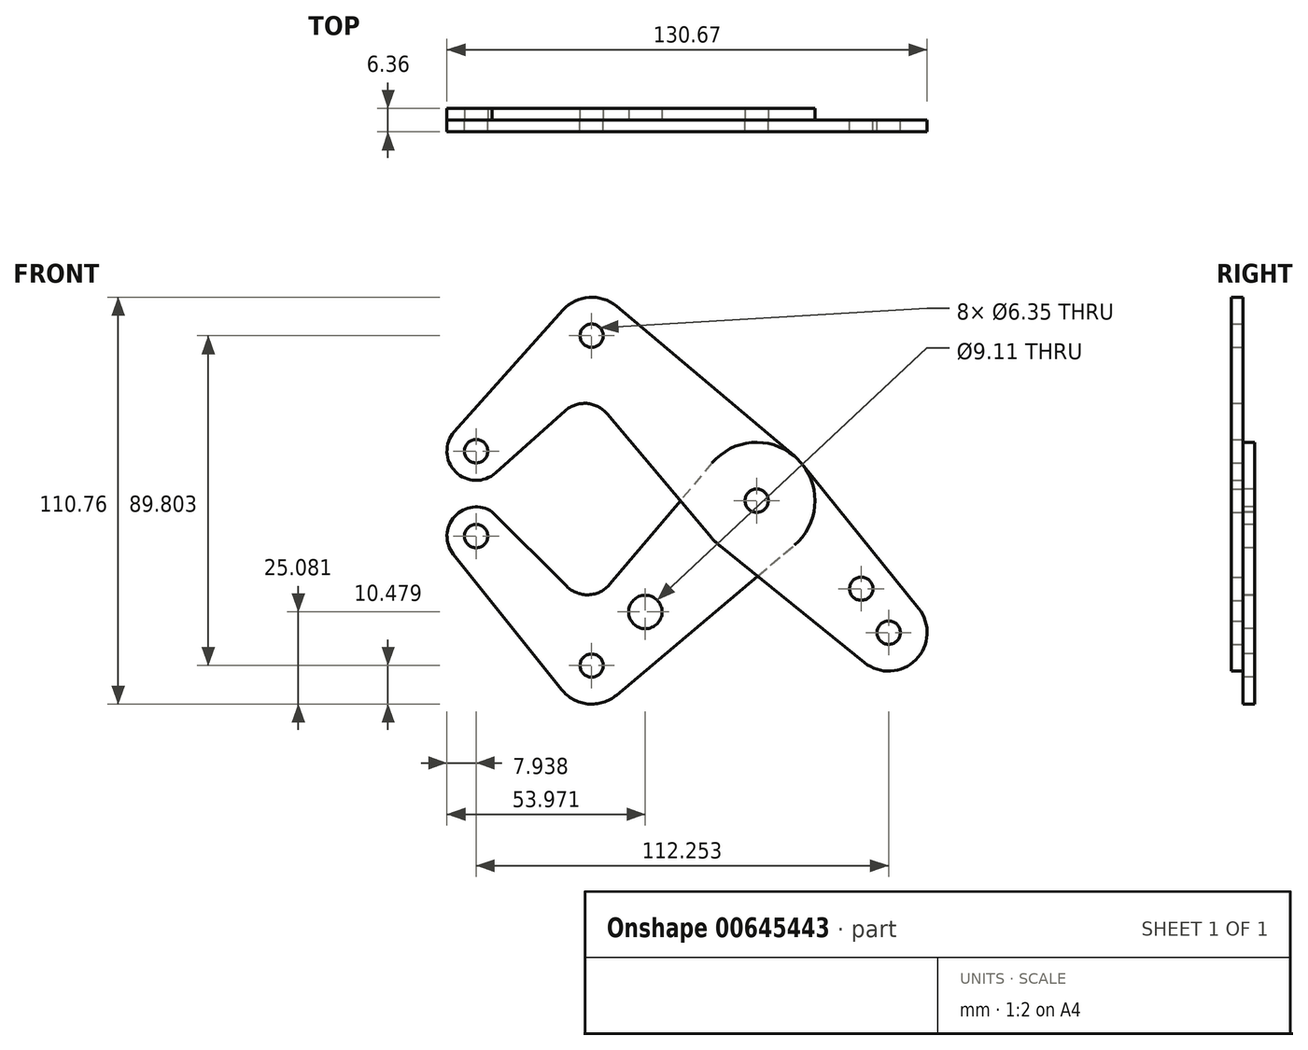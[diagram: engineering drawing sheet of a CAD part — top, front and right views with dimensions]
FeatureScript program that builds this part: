
annotation { "Feature Type Name" : "Feature", "Feature Type Description" : "" }
export const myFeature = defineFeature(function(context is Context, id is Id, definition is map)
    precondition{}
    {
        {
            var Q0;
            Q0=qCreatedBy(makeId("Front.planeOp"),FACE);
            var sketch = newSketch(context, id + "F0", { "sketchPlane" : qUnion([Q0])});
            skLineSegment(sketch, "E0", {"start": v(-76.33, 13.47) * mm, "end": v(-44.9, 44.9) * mm, "construction": true});
            skLineSegment(sketch, "E1", {"start": v(-44.9, 44.9) * mm, "end": v(35.92, -35.92) * mm, "construction": true});
            skCircle(sketch, "E2", {"center": v(-76.33, 13.47) * mm, "radius": 3.18 * mm});
            skCircle(sketch, "E3", {"center": v(-76.33, 13.47) * mm, "radius": 7.94 * mm});
            skCircle(sketch, "E4", {"center": v(-44.9, 44.9) * mm, "radius": 3.18 * mm});
            skCircle(sketch, "E5", {"center": v(-44.9, 44.9) * mm, "radius": 10.48 * mm});
            skCircle(sketch, "E6", {"center": v(0, 0) * mm, "radius": 3.18 * mm});
            skCircle(sketch, "E7", {"center": v(0, 0) * mm, "radius": 3.98 * mm});
            skCircle(sketch, "E8", {"center": v(0, 0) * mm, "radius": 15.88 * mm});
            skCircle(sketch, "E9", {"center": v(35.92, -35.92) * mm, "radius": 3.18 * mm});
            skCircle(sketch, "E10", {"center": v(35.92, -35.92) * mm, "radius": 10.48 * mm});
            skCircle(sketch, "E11", {"center": v(28.46, -23.97) * mm, "radius": 3.18 * mm});
            skLineSegment(sketch, "E12", {"start": v(-82.26, 18.75) * mm, "end": v(-52.72, 51.87) * mm});
            skLineSegment(sketch, "E13", {"start": v(-71.05, 7.55) * mm, "end": v(-52.07, 24.47) * mm});
            skLineSegment(sketch, "E14", {"start": v(-40.7, 23.66) * mm, "end": v(-12.14, -10.23) * mm});
            skLineSegment(sketch, "E15", {"start": v(12.35, 9.97) * mm, "end": v(44.07, -29.34) * mm});
            skLineSegment(sketch, "E16", {"start": v(-38.15, 52.91) * mm, "end": v(10.23, 12.14) * mm});
            skLineSegment(sketch, "E17", {"start": v(-9.97, -12.35) * mm, "end": v(29.34, -44.07) * mm});
            skLineSegment(sketch, "E18", {"start": v(0, 0) * mm, "end": v(23.84, 19.23) * mm, "construction": true});
            skArc(sketch, "E19.filletArc", {"start": v(-40.7, 23.66) * mm, "mid": v(-46.21, 26.47) * mm, "end": v(-52.07, 24.47) * mm});
            skLineSegment(sketch, "E20", {"start": v(0, 0) * mm, "end": v(-44.9, -44.9) * mm, "construction": true});
            skLineSegment(sketch, "E21", {"start": v(-44.9, -44.9) * mm, "end": v(-76.33, -9.65) * mm, "construction": true});
            skCircle(sketch, "E22", {"center": v(-44.9, -44.9) * mm, "radius": 3.18 * mm});
            skCircle(sketch, "E23", {"center": v(-44.9, -44.9) * mm, "radius": 10.48 * mm});
            skCircle(sketch, "E24", {"center": v(-30.3, -30.3) * mm, "radius": 4.55 * mm});
            skCircle(sketch, "E25", {"center": v(-76.33, -9.65) * mm, "radius": 3.18 * mm});
            skCircle(sketch, "E26", {"center": v(-76.33, -9.65) * mm, "radius": 7.94 * mm});
            skLineSegment(sketch, "E27", {"start": v(-82.53, -14.61) * mm, "end": v(-53.08, -51.44) * mm});
            skLineSegment(sketch, "E28", {"start": v(-71.95, -3.04) * mm, "end": v(-51.68, -23.3) * mm});
            skLineSegment(sketch, "E29", {"start": v(-38.15, -52.91) * mm, "end": v(10.23, -12.14) * mm});
            skLineSegment(sketch, "E30", {"start": v(-12.14, 10.23) * mm, "end": v(-39.98, -22.8) * mm});
            skArc(sketch, "E31.filletArc", {"start": v(-51.68, -23.3) * mm, "mid": v(-45.72, -25.62) * mm, "end": v(-39.98, -22.8) * mm});
            skSolve(sketch);
        }
        {
            var Q0;
            {var subQ0=sQuery(id+"F0.wireOp",EDGE,"E12");Q0=makeQuery(id+"F0.imprint","IMPRINT",FACE,{"disambiguationData":[TD([[makeQuery(id+"F0.imprint","IMPRINT",EDGE,{"derivedFrom":subQ0}),-1.0]])]});}
            var Q1;
            Q1=makeQuery(id+"F0.imprint","IMPRINT",FACE,{"disambiguationData":[TD([[makeQuery(id+"F0.imprint","IMPRINT",EDGE,{"derivedFrom":sQuery(id+"F0.wireOp",EDGE,"E2")}),-1.0]])]});
            var Q2;
            Q2=makeQuery(id+"F0.imprint","IMPRINT",FACE,{"disambiguationData":[TD([[makeQuery(id+"F0.imprint","IMPRINT",EDGE,{"derivedFrom":sQuery(id+"F0.wireOp",EDGE,"E4")}),-1.0]])]});
            var Q3;
            {var subQ0=sQuery(id+"F0.wireOp",EDGE,"E14");var subQ1=sQuery(id+"F0.wireOp",EDGE,"E8");var subQ2=makeQuery(id+"F0.imprint","INTERSECT",VERTEX,{"derivedFrom":[subQ1,subQ0]});Q3=makeQuery(id+"F0.imprint","IMPRINT",FACE,{"disambiguationData":[TD([[makeQuery(id+"F0.imprint","IMPRINT",EDGE,{"disambiguationData":[TD([[subQ2,1.0]])],"derivedFrom":subQ1}),-1.0]])]});}
            var Q4;
            {var subQ0=sQuery(id+"F0.wireOp",EDGE,"E17");var subQ1=sQuery(id+"F0.wireOp",EDGE,"E8");var subQ2=makeQuery(id+"F0.imprint","INTERSECT",VERTEX,{"derivedFrom":[subQ1,subQ0]});Q4=makeQuery(id+"F0.imprint","IMPRINT",FACE,{"disambiguationData":[TD([[makeQuery(id+"F0.imprint","IMPRINT",EDGE,{"disambiguationData":[TD([[subQ2,-1.0]])],"derivedFrom":subQ1}),-1.0]])]});}
            var Q5;
            Q5=makeQuery(id+"F0.imprint","IMPRINT",FACE,{"disambiguationData":[TD([[makeQuery(id+"F0.imprint","IMPRINT",EDGE,{"derivedFrom":sQuery(id+"F0.wireOp",EDGE,"E11")}),-1.0]])]});
            var Q6;
            Q6=makeQuery(id+"F0.imprint","IMPRINT",FACE,{"disambiguationData":[TD([[makeQuery(id+"F0.imprint","IMPRINT",EDGE,{"derivedFrom":sQuery(id+"F0.wireOp",EDGE,"E9")}),-1.0]])]});
            var Q7;
            Q7=makeQuery(id+"F0.imprint","IMPRINT",FACE,{"disambiguationData":[TD([[makeQuery(id+"F0.imprint","IMPRINT",EDGE,{"derivedFrom":sQuery(id+"F0.wireOp",EDGE,"E7")}),-1.0]])]});
            var Q8;
            Q8=makeQuery(id+"F0.imprint","IMPRINT",FACE,{"disambiguationData":[TD([[makeQuery(id+"F0.imprint","IMPRINT",EDGE,{"derivedFrom":sQuery(id+"F0.wireOp",EDGE,"E6")}),-1.0]])]});
            extrude(context, id + "F1", {"entities" : qUnion([Q0, Q1, Q2, Q3, Q4, Q5, Q6, Q7, Q8]), "depth" : 3.17 * mm, "offsetDistance" : 25.4 * mm});
        }
        {
            var Q0;
            {var subQ0=sQuery(id+"F0.wireOp",EDGE,"E27");Q0=makeQuery(id+"F0.imprint","IMPRINT",FACE,{"disambiguationData":[TD([[makeQuery(id+"F0.imprint","IMPRINT",EDGE,{"derivedFrom":subQ0}),1.0]])]});}
            var Q1;
            Q1=makeQuery(id+"F0.imprint","IMPRINT",FACE,{"disambiguationData":[TD([[makeQuery(id+"F0.imprint","IMPRINT",EDGE,{"derivedFrom":sQuery(id+"F0.wireOp",EDGE,"E25")}),-1.0]])]});
            var Q2;
            Q2=makeQuery(id+"F0.imprint","IMPRINT",FACE,{"disambiguationData":[TD([[makeQuery(id+"F0.imprint","IMPRINT",EDGE,{"derivedFrom":sQuery(id+"F0.wireOp",EDGE,"E24")}),-1.0]])]});
            var Q3;
            Q3=makeQuery(id+"F0.imprint","IMPRINT",FACE,{"disambiguationData":[TD([[makeQuery(id+"F0.imprint","IMPRINT",EDGE,{"derivedFrom":sQuery(id+"F0.wireOp",EDGE,"E22")}),-1.0]])]});
            var Q4;
            {var subQ0=sQuery(id+"F0.wireOp",EDGE,"E28");var subQ1=sQuery(id+"F0.wireOp",EDGE,"E23");var subQ2=makeQuery(id+"F0.imprint","INTERSECT",VERTEX,{"derivedFrom":[subQ1,subQ0]});Q4=makeQuery(id+"F0.imprint","IMPRINT",FACE,{"disambiguationData":[TD([[makeQuery(id+"F0.imprint","IMPRINT",EDGE,{"disambiguationData":[TD([[subQ2,-1.0]])],"derivedFrom":subQ1}),-1.0]])]});}
            var Q5;
            {var subQ0=sQuery(id+"F0.wireOp",EDGE,"E14");var subQ1=sQuery(id+"F0.wireOp",EDGE,"E8");var subQ2=makeQuery(id+"F0.imprint","INTERSECT",VERTEX,{"derivedFrom":[subQ1,subQ0]});Q5=makeQuery(id+"F0.imprint","IMPRINT",FACE,{"disambiguationData":[TD([[makeQuery(id+"F0.imprint","IMPRINT",EDGE,{"disambiguationData":[TD([[subQ2,1.0]])],"derivedFrom":subQ1}),-1.0]])]});}
            var Q6;
            {var subQ0=sQuery(id+"F0.wireOp",EDGE,"E17");var subQ1=sQuery(id+"F0.wireOp",EDGE,"E8");var subQ2=makeQuery(id+"F0.imprint","INTERSECT",VERTEX,{"derivedFrom":[subQ1,subQ0]});Q6=makeQuery(id+"F0.imprint","IMPRINT",FACE,{"disambiguationData":[TD([[makeQuery(id+"F0.imprint","IMPRINT",EDGE,{"disambiguationData":[TD([[subQ2,-1.0]])],"derivedFrom":subQ1}),-1.0]])]});}
            var Q7;
            Q7=makeQuery(id+"F0.imprint","IMPRINT",FACE,{"disambiguationData":[TD([[makeQuery(id+"F0.imprint","IMPRINT",EDGE,{"derivedFrom":sQuery(id+"F0.wireOp",EDGE,"E6")}),-1.0]])]});
            var Q8;
            Q8=makeQuery(id+"F0.imprint","IMPRINT",FACE,{"disambiguationData":[TD([[makeQuery(id+"F0.imprint","IMPRINT",EDGE,{"derivedFrom":sQuery(id+"F0.wireOp",EDGE,"E7")}),-1.0]])]});
            extrude(context, id + "F2", {"entities" : qUnion([Q0, Q1, Q2, Q3, Q4, Q5, Q6, Q7, Q8]), "oppositeDirection" : true, "depth" : 3.17 * mm, "offsetDistance" : 25.4 * mm});
        }
        {
            var Q0;
            Q0=makeQuery(id+"F1.opExtrude","CAP_FACE",FACE,{"disambiguationData":[OSD([sQuery(id+"F0.wireOp",EDGE,"E2"),sQuery(id+"F0.wireOp",EDGE,"E3"),sQuery(id+"F0.wireOp",EDGE,"E4"),sQuery(id+"F0.wireOp",EDGE,"E5"),sQuery(id+"F0.wireOp",EDGE,"E6"),sQuery(id+"F0.wireOp",EDGE,"E8"),sQuery(id+"F0.wireOp",EDGE,"E9"),sQuery(id+"F0.wireOp",EDGE,"E10"),sQuery(id+"F0.wireOp",EDGE,"E11"),sQuery(id+"F0.wireOp",EDGE,"E12"),sQuery(id+"F0.wireOp",EDGE,"E13"),sQuery(id+"F0.wireOp",EDGE,"E14"),sQuery(id+"F0.wireOp",EDGE,"E15"),sQuery(id+"F0.wireOp",EDGE,"E16"),sQuery(id+"F0.wireOp",EDGE,"E17"),sQuery(id+"F0.wireOp",EDGE,"E19.filletArc")])],"isStart":false});
            var sketch = newSketch(context, id + "F3", { "sketchPlane" : qUnion([Q0])});
            skCircle(sketch, "E32", {"center": v(-44.9, 44.9) * mm, "radius": 3.98 * mm});
            skCircle(sketch, "E33.0", {"center": v(35.92, -35.92) * mm, "radius": 10.48 * mm});
            skSolve(sketch);
        }
        {
            var Q0;
            Q0=qCreatedBy(makeId("Front.planeOp"),FACE);
            cPlane(context, id + "F4", {"entities" : qUnion([Q0]), "cplaneType" : CPlaneType.OFFSET, "offset" : 87.22 * mm, "width" : 152.4 * mm, "height" : 152.4 * mm});
        }
    });
